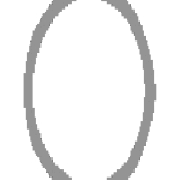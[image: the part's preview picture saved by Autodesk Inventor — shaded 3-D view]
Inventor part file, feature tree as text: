
AUTODESK INVENTOR PART (.ipt)
format: ipt  version: 2021 (Build 250183000, 183)  size: 111,616 bytes
history: native  units: in
note: dims shown in document units (in); Inventor stores cm internally (conversion verified against a paired STEP export)
features: other x4, sketch x3, plane x1
ambient origin geometry x8: Origin, YZ Plane, XZ Plane, XY Plane, X Axis, Y Axis, Z Axis, Center Point
bodies: Solid1 (feature_tree), Body (feature_tree)
feature tree (8):
  other  "Driven Length"
  other  "Frame Generator"
  other  "Start Plane"
  other  "End Plane"
  sketch  "Sketch"  dims[d2=23.8537in d4=-0.0in d5=23.8537in d6=0.12in d7=0.0in d8=90.0deg d9=23.8537in]
  sketch  "Sketch2"  dims[d0=1.0in]
  plane  "Work Plane3"
  sketch  "Sketch3"  dims[d1=0.065in]
